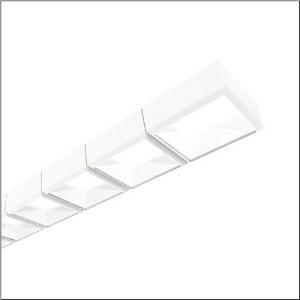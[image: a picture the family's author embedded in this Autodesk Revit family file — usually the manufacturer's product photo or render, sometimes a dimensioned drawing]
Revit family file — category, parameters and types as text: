
# Revit family: scriptus_r__11_5mz323d04wa_1206
name_source: partatom
category: Lighting Fixtures
units: mm (PartAtom-declared; Revit-internal decimal feet)

## family parameters
Cut with Voids When Loaded = No
Host = Face
Light Source = No
Part Type = Normal
Room Calculation Point = No
Round Connector Dimension = Use Diameter
Shared = No

## types (1)
- Scriptus® 11 (1 x LED 4000K / CRI = 80 (unbekannt), 4840 lm / 7230 lm, 4000K)
    Apparent Load = 91 VA
    CIE Flux Codes = - - - 0 100 / 82 95 99 100 100
    Color Rendering = 80
    Color Temperature = 4000K
    Default Elevation = 1800 mm
    Description = Scriptus® 11, office luminaire, primary optical cover: lenses, CAT 2 (L<= 3000cd/m²), light emission: direct/indirect distribution, primary light characteristic: symmetric, installation type: suspended mounting, LED, rated luminous flux: 12.070lm, luminous efficacy: 133lm/W, light colour: 840, colour temperature: 4000K, control gear: DALI, with terminal, 5-pole, mains connection: 230V, AC, 50Hz, rated input power: 91W, LED, control gear: ECG DALI, housing, luminaire housing, of aluminium, traffic white (RAL 9016), length: 2.426mm, width: 114mm, height: 57mm, protection rating (complete): IP20, insulation class (complete): insulation class I (protective earthing), certification: CE, ENEC, VDE, protection symbol: F, permissible operating ambient temperature: 0..+35°C, standard: EN 50419, packaging unit: 1 piece
    Height = 57 mm
    Lamp = 1 x LED 4000K / CRI >= 80 (unbekannt)
    Lamp Light Flux = 4840 lm / 7230 lm
    Lamp count = 1
    Length = 2426 mm
    Luminous efficacy = 133 lm/W
    Manufacturer = Siteco
    ModVariant = No
    Model = 5MZ323D04WA
    Mounting Place = Ceiling
    Mounting Type = Pendant
    Number of Poles = 1
    OnlyDefault = Yes
    Power Factor = 1
    Product Name = Scriptus® 11
    Product group = office luminaire | ceiling pendant
    ProductGroupID = 904
    Protection Class = Protection class I
    Protection Degree = IP 20
    RLX_Detail_Level = 1
    RLX_Emergency_Light_Flux = 0 lm
    RLX_Emergency_Type = 0
    RLX_Emergency_Type_DB = No
    RlxData = <blob elided: 30249 chars, md5=94bf5312>
    Socket = socket
    Standby Power = 0 W
    System Light Flux = 12070 lm
    System Power = 91 W
    Type Comments = Product without accessories
    Type Image = l_1004839.jpg
    URL = http://relux.com
    VarID = ---
    Voltage = 0 V
    Weight = 0.00 kg
    Width = 114 mm

## geometry (parser evidence)
native form markers: Blend x4, Sweep x14
no freeform markers — native parametric forms only
